# Revit family: OWEZV  12'' GLASS
name_source: partatom
category: Mechanical Equipment
units: mm (PartAtom-declared; Revit-internal decimal feet)

## family parameters
Always vertical = Yes
Cut with Voids When Loaded = No
OmniClass Number = 23.40.40.11.17
OmniClass Title = Refrigerated Cases
Part Type = Normal
Room Calculation Point = No
Round Connector Dimension = Use Radius
Shared = No
Work Plane-Based = Yes

## types (6) — shared parameters
BOTTOM ELECTRICAL = Yes
BOTTOM REFRIGERATION PIPING = Yes
CENTER LINE = 48"
Certifications = NSF 7, UL471, CSA
DATE = 04/11/2016
DRAIN LINE CONNECTION = SANITARY CONNECTION
DRAIN LINE DIAMETER = 2"
DRAIN PIPE TYPE = PVC
DRAIN PIPING = Yes
DRIP PAN PLUMB TYPE = HARD
Default Elevation = 48"
Description = OWEZV end case
EQUIPMENT DESCRIPTION = OWEZV end case
EQUIPMENT MARK = OWEZV
Height = 36 1/8"
How Many Defrosts Per Day = 1
Island  Case Length = 96"
Island 208V Defrost Heaters Amps = 9 A
Island 208V Defrost Heaters Watts = 1800 A
Island 240 Defrost Heaters Amps = 10 A
Island 240 Defrost Heaters Watts = 2394 W
Island Anti-Condensate Heaters Amps = 1 A
Island Discharge Air Velocity (FPM) = 200 FPM
Island Electric Termination Temp (F°) = 49 °F
Island Fans Per Case = 2
Island High Efficiency Fans Amps = 0 A
Island High Efficiency Fans Watts = 8 W
Island Hot Gas Termination Temp (F°) = 60 °F
Island Tank/Drain Heater Amps = 0 A
Island Tank/Drain Heater Watts = 15 W
Item Description = OWEZV end case
LF STD END = Yes
LIQUID LINE CONNECTION = LIQUID LINE CONNECTION
LIQUID LINE DIAMETER = 0"
LIQUID LINE RADIUS = 0"
Legend Number = OWEZV
Length = 96"
Manufacturer = HILL PHOENIX
Model = OWEZV
PRESSURE REGULATOR = 0.00 psi
RT STD END = Yes
SANITARY PIPE SIZE = 1"
SUCTION LINE CONNECTION = SUCTION LINE CONNECTION
SUCTION LINE DIAMETER = 1"
SUCTION LINE RADIUS = 0"
URL = http://www.hillphoenix.com
Width = 84 1/4"

## per-type parameters (varying)
| type | Case Type/Application | Island Anti-Condensate Heaters Watts | Island Application | Island BTUH Conventional | Island BTUH Parallel | Island Discharge Air(°F) | Island Electric Fail-Safe | Island Electric Run-Off Time (Min) | Island Evaporator (°F) | Island Hot Gas Fail-Safe (Min) | Island Hot Gas Run-Off Time (Min) | Island Superheat @ Bulb Set Point (°F) | Island Timed-Off Fail-Safe (Min) | Island Timed-Off Termination Temp (°F) |
| 08' - Medium Temp - Solid Front | Medium Temp | 98 W | Medium Temp | 1038 | 1008 | 27 °F | 35 (Min) | 0 (Min) | 17 °F | 10 (Min) | 0 (Min) | 6-8 °F | 32 (Min) | 42 °F |
| 08' - Frozen Food - Solid Front | Frozen Food | 98 W | Frozen Food | 1726 | 1689 | -6 °F | 60 (Min) | 5 (Min) | -12 °F | 20 (Min) | 13-15 (Min) | 3-5 °F | 0 | 0 °F |
| 08' - Ice Cream - Solid Front | Frozen Food | 98 W | Ice Cream | 1956 | 1900 | -16 °F | 60 (Min) | 5 (Min) | -22 °F | 20 (Min) | 13-15 (Min) | 3-5 °F | 0 | 0 °F |
| 08' - Medium Temp - Glass Front | Medium Temp | 178 W | Medium Temp | 2196 | 2196 | 27 °F | 35 (Min) | 0 (Min) | 17 °F | 10 (Min) | 0 (Min) | 6-8 °F | 32 (Min) | 42 °F |
| 08' - Frozen Food - Glass Front | Frozen Food | 178 W | Frozen Food | 2769 | 2663 | -6 °F | 60 (Min) | 5 (Min) | -12 °F | 20 (Min) | 13-15 (Min) | 3-5 °F | 0 | 0 °F |
| 08' - Ice Cream - Glass Front | Frozen Food | 178 W | Ice Cream | 3429 | 3429 | -16 °F | 60 (Min) | 5 (Min) | -22 °F | 20 (Min) | 13-15 (Min) | 3-5 °F | 0 | 0 °F |

## geometry (parser evidence)
native form markers: Blend x8, Sweep x2
no freeform markers — native parametric forms only
